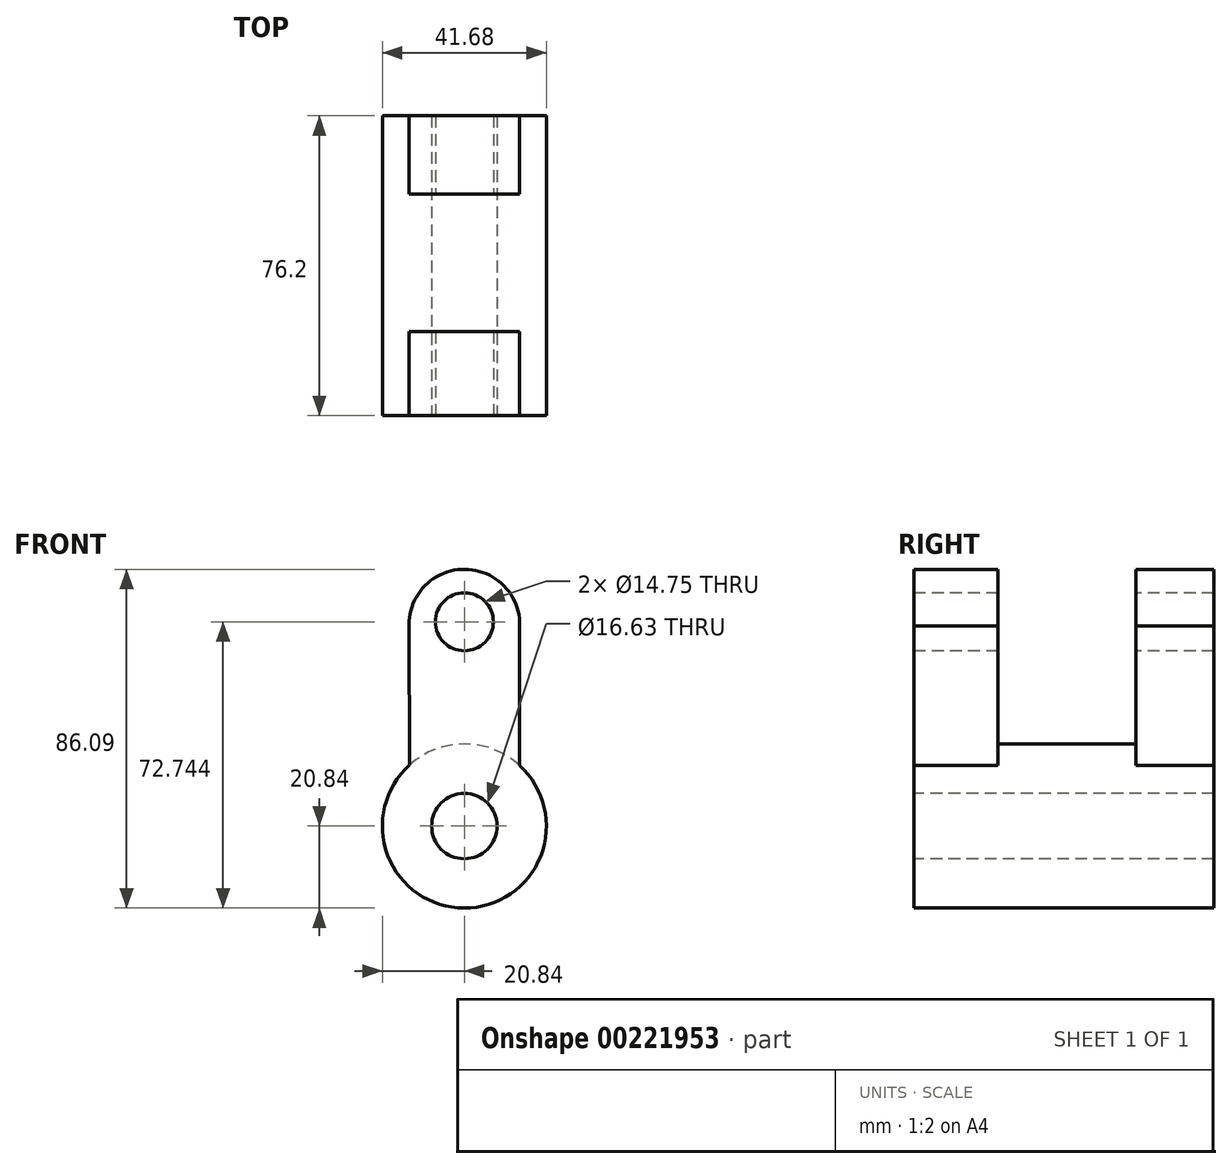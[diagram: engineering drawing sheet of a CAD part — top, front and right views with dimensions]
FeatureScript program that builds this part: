
annotation { "Feature Type Name" : "Feature", "Feature Type Description" : "" }
export const myFeature = defineFeature(function(context is Context, id is Id, definition is map)
    precondition{}
    {
        {
            var Q0;
            Q0=qCreatedBy(makeId("Front.planeOp"),FACE);
            var sketch = newSketch(context, id + "F0", { "sketchPlane" : qUnion([Q0])});
            skCircle(sketch, "E0", {"center": v(0, 51.2) * mm, "radius": 14.05 * mm});
            skLineSegment(sketch, "E1", {"start": v(-14.05, 51.14) * mm, "end": v(-13.79, -12.98) * mm});
            skLineSegment(sketch, "E2", {"start": v(-13.79, -12.98) * mm, "end": v(14.04, -12.98) * mm});
            skLineSegment(sketch, "E3", {"start": v(14.04, -12.98) * mm, "end": v(14.04, 50.9) * mm});
            skLineSegment(sketch, "E4", {"start": v(14.04, 50.9) * mm, "end": v(-14.05, 51.14) * mm});
            skSolve(sketch);
        }
        {
            var Q0;
            Q0 = qSketchRegion(id + "F0", true);
            extrude(context, id + "F1", {"entities" : qUnion([Q0]), "depth" : 38.1 * mm, "hasSecondDirection" : true, "secondDirectionOppositeDirection" : true, "secondDirectionDepth" : 38.1 * mm});
        }
        {
            var Q0;
            Q0=qCreatedBy(makeId("Right.planeOp"),FACE);
            var sketch = newSketch(context, id + "F2", { "sketchPlane" : qUnion([Q0])});
            skLineSegment(sketch, "E5", {"start": v(-16.73, 70.6) * mm, "end": v(-16.73, 12.96) * mm});
            skLineSegment(sketch, "E6", {"start": v(-16.73, 12.96) * mm, "end": v(18.26, 12.96) * mm});
            skLineSegment(sketch, "E7", {"start": v(18.26, 12.96) * mm, "end": v(18.26, 70.6) * mm});
            skLineSegment(sketch, "E8", {"start": v(18.26, 70.6) * mm, "end": v(-16.73, 70.6) * mm});
            skSolve(sketch);
        }
        {
            var Q0;
            Q0 = qSketchRegion(id + "F2", true);
            extrude(context, id + "F3", {"entities" : qUnion([Q0]), "operationType" : NewBodyOperationType.REMOVE, "endBound" : BoundingType.THROUGH_ALL, "oppositeDirection" : true, "depth" : 25.4 * mm, "hasSecondDirection" : true, "secondDirectionOppositeDirection" : false, "secondDirectionDepth" : 25.4 * mm});
        }
        {
            var Q0;
            Q0=qCreatedBy(makeId("Front.planeOp"),FACE);
            var sketch = newSketch(context, id + "F4", { "sketchPlane" : qUnion([Q0])});
            skCircle(sketch, "E9", {"center": v(0, 0) * mm, "radius": 20.84 * mm});
            skSolve(sketch);
        }
        {
            var Q0;
            Q0 = qSketchRegion(id + "F4", true);
            extrude(context, id + "F5", {"entities" : qUnion([Q0]), "operationType" : NewBodyOperationType.ADD, "depth" : 25.4 * mm});
        }
        {
            var Q0;
            Q0 = qSketchRegion(id + "F4", true);
            extrude(context, id + "F6", {"entities" : qUnion([Q0]), "operationType" : NewBodyOperationType.ADD, "depth" : 38.1 * mm, "hasSecondDirection" : true, "secondDirectionOppositeDirection" : true, "secondDirectionDepth" : 38.1 * mm});
        }
        {
            var Q0;
            Q0=qCreatedBy(makeId("Front.planeOp"),FACE);
            var sketch = newSketch(context, id + "F7", { "sketchPlane" : qUnion([Q0])});
            skCircle(sketch, "E10", {"center": v(0, 0) * mm, "radius": 8.32 * mm});
            skCircle(sketch, "E11", {"center": v(0, 51.9) * mm, "radius": 7.38 * mm});
            skSolve(sketch);
        }
        {
            var Q0;
            Q0 = qSketchRegion(id + "F7", true);
            extrude(context, id + "F8", {"entities" : qUnion([Q0]), "operationType" : NewBodyOperationType.REMOVE, "endBound" : BoundingType.THROUGH_ALL, "oppositeDirection" : true, "depth" : 25.4 * mm, "hasSecondDirection" : true, "secondDirectionBound" : SecondDirectionBoundingType.THROUGH_ALL, "secondDirectionOppositeDirection" : false, "secondDirectionDepth" : 25.4 * mm});
        }
    });
